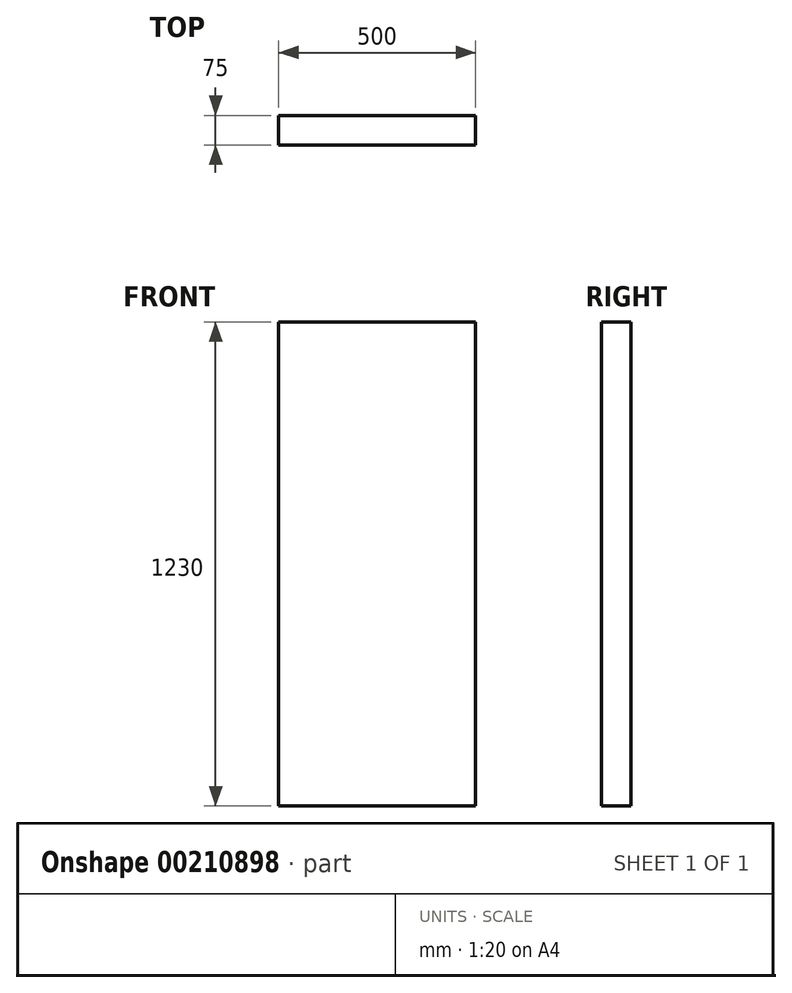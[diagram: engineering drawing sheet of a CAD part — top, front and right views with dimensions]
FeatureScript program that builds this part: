
annotation { "Feature Type Name" : "Feature", "Feature Type Description" : "" }
export const myFeature = defineFeature(function(context is Context, id is Id, definition is map)
    precondition{}
    {
        {
            var Q0;
            Q0=qCreatedBy(makeId("Front.planeOp"),FACE);
            var sketch = newSketch(context, id + "F0", { "sketchPlane" : qUnion([Q0])});
            skLineSegment(sketch, "E0.bottom", {"start": v(0, 0) * mm, "end": v(500, 0) * mm});
            skLineSegment(sketch, "E0.top", {"start": v(0, 1230) * mm, "end": v(500, 1230) * mm});
            skLineSegment(sketch, "E0.left", {"start": v(0, 0) * mm, "end": v(0, 1230) * mm});
            skLineSegment(sketch, "E0.right", {"start": v(500, 0) * mm, "end": v(500, 1230) * mm});
            skSolve(sketch);
        }
        {
            var Q0;
            Q0=makeQuery(id+"F0.imprint","IMPRINT",FACE,{"disambiguationData":[TD([[makeQuery(id+"F0.imprint","IMPRINT",EDGE,{"derivedFrom":sQuery(id+"F0.wireOp",EDGE,"E0.bottom")}),1.0]])]});
            extrude(context, id + "F1", {"entities" : qUnion([Q0]), "depth" : 75 * mm});
        }
    });
